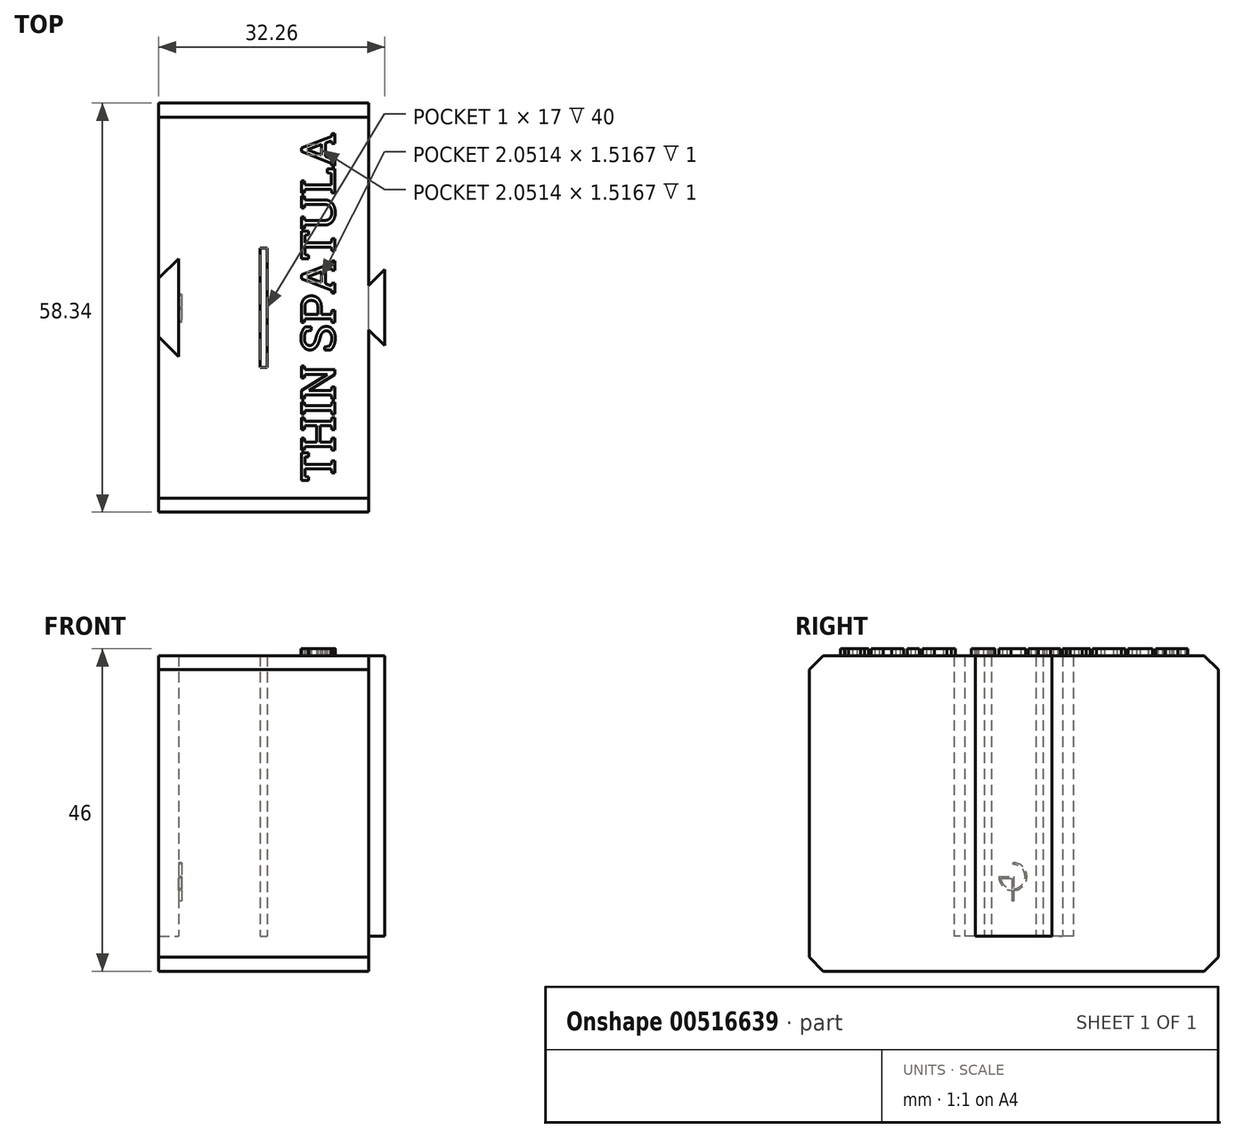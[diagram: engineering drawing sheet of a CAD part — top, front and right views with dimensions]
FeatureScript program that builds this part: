
annotation { "Feature Type Name" : "Feature", "Feature Type Description" : "" }
export const myFeature = defineFeature(function(context is Context, id is Id, definition is map)
    precondition{}
    {
        {
            var Q0;
            Q0=qCreatedBy(makeId("Top.planeOp"),FACE);
            var sketch = newSketch(context, id + "F0", { "sketchPlane" : qUnion([Q0])});
            skLineSegment(sketch, "E0", {"start": v(-15, 4.17) * mm, "end": v(-15, 29.17) * mm});
            skLineSegment(sketch, "E1", {"start": v(-15, 29.17) * mm, "end": v(15, 29.17) * mm});
            skLineSegment(sketch, "E2", {"start": v(15, 29.17) * mm, "end": v(15, 3.17) * mm});
            skLineSegment(sketch, "E3", {"start": v(-15, 4.17) * mm, "end": v(-12.17, 7) * mm});
            skLineSegment(sketch, "E4", {"start": v(-12.17, 7) * mm, "end": v(-12.17, 0) * mm});
            skLineSegment(sketch, "E5", {"start": v(15, 3.17) * mm, "end": v(17.26, 5.43) * mm});
            skLineSegment(sketch, "E6", {"start": v(17.26, 5.43) * mm, "end": v(17.26, -0.57) * mm});
            skLineSegment(sketch, "E7.MirrorCS", {"start": v(-15, -4.17) * mm, "end": v(-12.17, -7) * mm});
            skLineSegment(sketch, "E8.MirrorCS", {"start": v(15, -29.17) * mm, "end": v(15, -3.17) * mm});
            skLineSegment(sketch, "E9.MirrorCS", {"start": v(-12.17, -7) * mm, "end": v(-12.17, 0) * mm});
            skLineSegment(sketch, "E10.MirrorCS", {"start": v(-15, -4.17) * mm, "end": v(-15, -29.17) * mm});
            skLineSegment(sketch, "E11.MirrorCS", {"start": v(17.26, -5.43) * mm, "end": v(17.26, 0.57) * mm});
            skLineSegment(sketch, "E12.MirrorCS", {"start": v(15, -3.17) * mm, "end": v(17.26, -5.43) * mm});
            skLineSegment(sketch, "E13.MirrorCS", {"start": v(-15, -29.17) * mm, "end": v(15, -29.17) * mm});
            skLineSegment(sketch, "E14.bottom", {"start": v(-0.5, 8.5) * mm, "end": v(0.5, 8.5) * mm});
            skLineSegment(sketch, "E14.top", {"start": v(-0.5, -8.5) * mm, "end": v(0.5, -8.5) * mm});
            skLineSegment(sketch, "E14.left", {"start": v(-0.5, 8.5) * mm, "end": v(-0.5, -8.5) * mm});
            skLineSegment(sketch, "E14.right", {"start": v(0.5, 8.5) * mm, "end": v(0.5, -8.5) * mm});
            skPoint(sketch, "E14.middle", {"position": v(0, 0) * mm});
            skLineSegment(sketch, "E15", {"start": v(-15, 4.17) * mm, "end": v(-15, -4.17) * mm});
            skLineSegment(sketch, "E16", {"start": v(15, 3.17) * mm, "end": v(15, -3.17) * mm});
            skSolve(sketch);
        }
        {
            var Q0;
            Q0=makeQuery(id+"F0.imprint","IMPRINT",FACE,{"disambiguationData":[TD([[makeQuery(id+"F0.imprint","IMPRINT",EDGE,{"derivedFrom":sQuery(id+"F0.wireOp",EDGE,"E5")}),-1.0]])]});
            var Q1;
            Q1=makeQuery(id+"F0.imprint","IMPRINT",FACE,{"disambiguationData":[TD([[makeQuery(id+"F0.imprint","IMPRINT",EDGE,{"derivedFrom":sQuery(id+"F0.wireOp",EDGE,"E0")}),-1.0]])]});
            extrude(context, id + "F1", {"entities" : qUnion([Q0, Q1]), "depth" : 40 * mm, "offsetDistance" : 25 * mm});
        }
        {
            var Q0;
            Q0=makeQuery(id+"F0.imprint","IMPRINT",FACE,{"disambiguationData":[TD([[makeQuery(id+"F0.imprint","IMPRINT",EDGE,{"derivedFrom":sQuery(id+"F0.wireOp",EDGE,"E0")}),-1.0]])]});
            var Q1;
            Q1=makeQuery(id+"F0.imprint","IMPRINT",FACE,{"disambiguationData":[TD([[makeQuery(id+"F0.imprint","IMPRINT",EDGE,{"derivedFrom":sQuery(id+"F0.wireOp",EDGE,"E14.bottom")}),-1.0]])]});
            var Q2;
            Q2=makeQuery(id+"F1.opExtrude","CAP_FACE",FACE,{"disambiguationData":[OSD([sQuery(id+"F0.wireOp",EDGE,"E0"),sQuery(id+"F0.wireOp",EDGE,"E1"),sQuery(id+"F0.wireOp",EDGE,"E2"),sQuery(id+"F0.wireOp",EDGE,"E5"),sQuery(id+"F0.wireOp",EDGE,"E6"),sQuery(id+"F0.wireOp",EDGE,"E8.MirrorCS"),sQuery(id+"F0.wireOp",EDGE,"E10.MirrorCS"),sQuery(id+"F0.wireOp",EDGE,"E11.MirrorCS"),sQuery(id+"F0.wireOp",EDGE,"E12.MirrorCS"),sQuery(id+"F0.wireOp",EDGE,"E13.MirrorCS"),sQuery(id+"F0.wireOp",EDGE,"E14.bottom"),sQuery(id+"F0.wireOp",EDGE,"E14.top"),sQuery(id+"F0.wireOp",EDGE,"E14.left"),sQuery(id+"F0.wireOp",EDGE,"E14.right"),sQuery(id+"F0.wireOp",EDGE,"E15")])],"isStart":false});
            var Q3;
            Q3=makeQuery(id+"F0.imprint","IMPRINT",FACE,{"disambiguationData":[TD([[makeQuery(id+"F0.imprint","IMPRINT",EDGE,{"derivedFrom":sQuery(id+"F0.wireOp",EDGE,"E3")}),-1.0]])]});
            extrude(context, id + "F2", {"entities" : qUnion([Q0, Q1, Q2, Q3]), "operationType" : NewBodyOperationType.ADD, "oppositeDirection" : true, "depth" : 5 * mm, "offsetDistance" : 25 * mm});
        }
        {
            var Q0;
            Q0=makeQuery(id+"F2.opExtrude","CAP_EDGE",EDGE,{"disambiguationData":[OSD([sQuery(id+"F0.wireOp",EDGE,"E13.MirrorCS")])],"isStart":false});
            var Q1;
            Q1=makeQuery(id+"F2.opExtrude","CAP_EDGE",EDGE,{"disambiguationData":[OSD([sQuery(id+"F0.wireOp",EDGE,"E1")])],"isStart":false});
            var Q2;
            Q2=makeQuery(id+"F1.opExtrude","CAP_EDGE",EDGE,{"disambiguationData":[OSD([sQuery(id+"F0.wireOp",EDGE,"E13.MirrorCS")])],"isStart":false});
            var Q3;
            Q3=makeQuery(id+"F1.opExtrude","CAP_EDGE",EDGE,{"disambiguationData":[OSD([sQuery(id+"F0.wireOp",EDGE,"E1")])],"isStart":false});
            chamfer(context, id + "F3", {"entities" : qUnion([Q0, Q1, Q2, Q3]), "width" : 2 * mm, "tangentPropagation" : true});
        }
        {
            var Q0;
            Q0=makeQuery(id+"F1.opExtrude","CAP_FACE",FACE,{"disambiguationData":[OSD([sQuery(id+"F0.wireOp",EDGE,"E0"),sQuery(id+"F0.wireOp",EDGE,"E1"),sQuery(id+"F0.wireOp",EDGE,"E2"),sQuery(id+"F0.wireOp",EDGE,"E3"),sQuery(id+"F0.wireOp",EDGE,"E4"),sQuery(id+"F0.wireOp",EDGE,"E5"),sQuery(id+"F0.wireOp",EDGE,"E6"),sQuery(id+"F0.wireOp",EDGE,"E7.MirrorCS"),sQuery(id+"F0.wireOp",EDGE,"E8.MirrorCS"),sQuery(id+"F0.wireOp",EDGE,"E9.MirrorCS"),sQuery(id+"F0.wireOp",EDGE,"E10.MirrorCS"),sQuery(id+"F0.wireOp",EDGE,"E11.MirrorCS"),sQuery(id+"F0.wireOp",EDGE,"E12.MirrorCS"),sQuery(id+"F0.wireOp",EDGE,"E13.MirrorCS"),sQuery(id+"F0.wireOp",EDGE,"E14.bottom"),sQuery(id+"F0.wireOp",EDGE,"E14.top"),sQuery(id+"F0.wireOp",EDGE,"E14.left"),sQuery(id+"F0.wireOp",EDGE,"E14.right")])],"isStart":false});
            var sketch = newSketch(context, id + "F4", { "sketchPlane" : qUnion([Q0])});
            skText(sketch, "E17", { "text": "THIN SPATULA", "fontName": "RobotoSlab-Regular.ttf"});
            const initialGuessF4  = {"E17": [0.01014, -0.0248, 0, 1, 0.00484]};
            skSetInitialGuess(sketch, initialGuessF4);
            skSolve(sketch);
        }
        {
            var Q0;
            Q0=qSketchRegion(id+"F4",true);
            extrude(context, id + "F5", {"entities" : qUnion([Q0]), "operationType" : NewBodyOperationType.ADD, "depth" : 1 * mm});
        }
        {
            var Q0;
            Q0=makeQuery(id+"F1.opExtrude","SWEPT_FACE",FACE,{"disambiguationData":[OSD([sQuery(id+"F0.wireOp",EDGE,"E4"),sQuery(id+"F0.wireOp",EDGE,"E9.MirrorCS")])]});
            var sketch = newSketch(context, id + "F6", { "sketchPlane" : qUnion([Q0])});
            skLineSegment(sketch, "E18.bottom", {"start": v(0.12, 10.5) * mm, "end": v(2.12, 10.5) * mm, "construction": true});
            skLineSegment(sketch, "E18.top", {"start": v(0.12, 8.5) * mm, "end": v(2.12, 8.5) * mm, "construction": true});
            skLineSegment(sketch, "E18.left", {"start": v(0.12, 10.5) * mm, "end": v(0.12, 8.5) * mm, "construction": true});
            skLineSegment(sketch, "E18.right", {"start": v(2.12, 10.5) * mm, "end": v(2.12, 8.5) * mm, "construction": true});
            skArc(sketch, "E19", {"start": v(0.12, 10.5) * mm, "mid": v(-1.3, 7.09) * mm, "end": v(2.12, 8.5) * mm});
            skLineSegment(sketch, "E20", {"start": v(0.12, 10.5) * mm, "end": v(0.12, 10.25) * mm});
            skLineSegment(sketch, "E21", {"start": v(2.12, 8.5) * mm, "end": v(1.87, 8.5) * mm});
            skArc(sketch, "E22", {"start": v(0.12, 10.25) * mm, "mid": v(-1.12, 7.26) * mm, "end": v(1.87, 8.5) * mm});
            skLineSegment(sketch, "E23", {"start": v(1.87, 8.5) * mm, "end": v(0, 8.5) * mm});
            skLineSegment(sketch, "E24", {"start": v(0, 8.5) * mm, "end": v(0, 5) * mm});
            skLineSegment(sketch, "E25", {"start": v(0, 5) * mm, "end": v(0.25, 5) * mm});
            skLineSegment(sketch, "E26", {"start": v(1.85, 8.25) * mm, "end": v(0.25, 8.25) * mm});
            skLineSegment(sketch, "E27", {"start": v(0.25, 8.25) * mm, "end": v(0.25, 5) * mm});
            skSolve(sketch);
        }
        {
            var Q0;
            {var subQ0=sQuery(id+"F6.wireOp",EDGE,"E20");Q0=makeQuery(id+"F6.imprint","IMPRINT",FACE,{"disambiguationData":[TD([[makeQuery(id+"F6.imprint","IMPRINT",EDGE,{"derivedFrom":subQ0}),-1.0]])]});}
            var Q1;
            {var subQ0=sQuery(id+"F6.wireOp",EDGE,"E24");var subQ1=sQuery(id+"F6.wireOp",EDGE,"E19");var subQ2=makeQuery(id+"F6.imprint","INTERSECT",VERTEX,{"derivedFrom":[subQ1,subQ0]});Q1=makeQuery(id+"F6.imprint","IMPRINT",FACE,{"disambiguationData":[TD([[makeQuery(id+"F6.imprint","IMPRINT",EDGE,{"disambiguationData":[TD([[subQ2,-1.0]])],"derivedFrom":subQ1}),1.0]])]});}
            var Q2;
            {var subQ5=sQuery(id+"F6.wireOp",EDGE,"E25");Q2=makeQuery(id+"F6.imprint","IMPRINT",FACE,{"disambiguationData":[TD([[makeQuery(id+"F6.imprint","IMPRINT",EDGE,{"derivedFrom":subQ5}),1.0]])]});}
            var Q3;
            {var subQ1=sQuery(id+"F6.wireOp",EDGE,"E21");Q3=makeQuery(id+"F6.imprint","IMPRINT",FACE,{"disambiguationData":[TD([[makeQuery(id+"F6.imprint","IMPRINT",EDGE,{"derivedFrom":subQ1}),1.0]])]});}
            var Q4;
            {var subQ1=sQuery(id+"F6.wireOp",EDGE,"E23");Q4=makeQuery(id+"F6.imprint","IMPRINT",FACE,{"disambiguationData":[TD([[makeQuery(id+"F6.imprint","IMPRINT",EDGE,{"derivedFrom":subQ1}),1.0]])]});}
            extrude(context, id + "F7", {"entities" : qUnion([Q0, Q1, Q2, Q3, Q4]), "operationType" : NewBodyOperationType.REMOVE, "oppositeDirection" : true, "depth" : .5 * mm, "offsetDistance" : 25 * mm});
        }
    });
